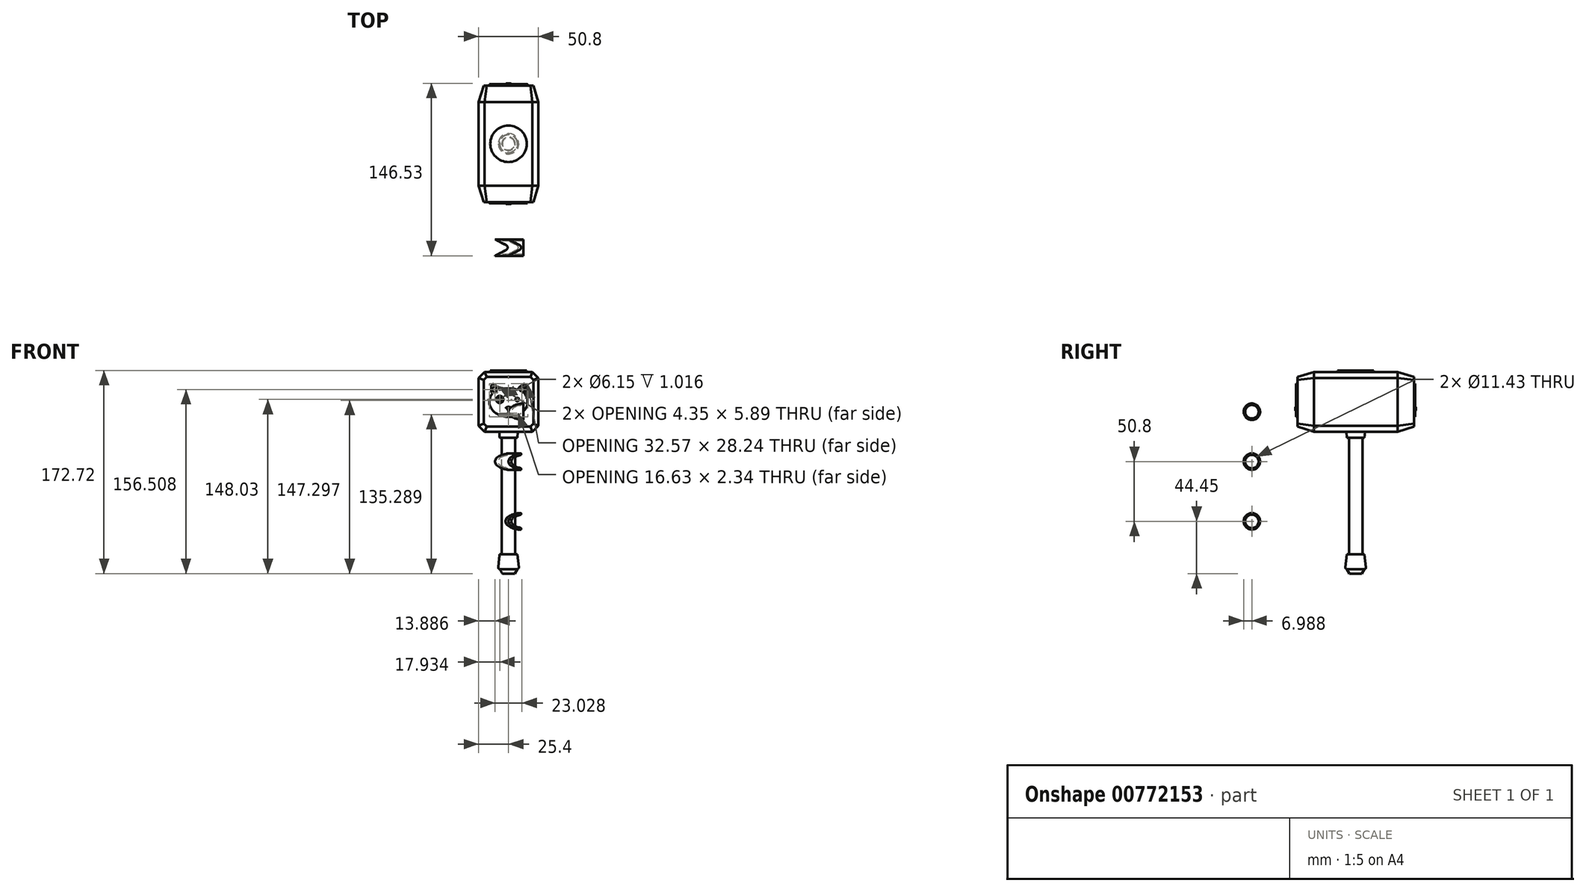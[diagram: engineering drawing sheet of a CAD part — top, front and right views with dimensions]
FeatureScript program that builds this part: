
annotation { "Feature Type Name" : "Feature", "Feature Type Description" : "" }
export const myFeature = defineFeature(function(context is Context, id is Id, definition is map)
    precondition{}
    {
        {
            var Q0;
            Q0=qCreatedBy(makeId("Front.planeOp"),FACE);
            var sketch = newSketch(context, id + "F0", { "sketchPlane" : qUnion([Q0])});
            skLineSegment(sketch, "E0.rect.bottom", {"start": v(25.4, 25.4) * mm, "end": v(-25.4, 25.4) * mm});
            skLineSegment(sketch, "E0.rect.top", {"start": v(25.4, -25.4) * mm, "end": v(-25.4, -25.4) * mm});
            skLineSegment(sketch, "E0.rect.left", {"start": v(25.4, 25.4) * mm, "end": v(25.4, -25.4) * mm});
            skLineSegment(sketch, "E0.rect.right", {"start": v(-25.4, 25.4) * mm, "end": v(-25.4, -25.4) * mm});
            skPoint(sketch, "E0.rect.middle", {"position": v(0, 0) * mm});
            skSolve(sketch);
        }
        {
            var Q0;
            Q0=makeQuery(id+"F0.imprint","IMPRINT",FACE,{"disambiguationData":[TD([[makeQuery(id+"F0.imprint","IMPRINT",EDGE,{"derivedFrom":sQuery(id+"F0.wireOp",EDGE,"E0.rect.bottom")}),1.0]])]});
            extrude(context, id + "F1", {"entities" : qUnion([Q0]), "endBound" : BoundingType.SYMMETRIC, "depth" : 71.12 * mm});
        }
        {
            var Q0;
            Q0=makeQuery(id+"F1.opExtrude","SWEPT_EDGE",EDGE,{"disambiguationData":[OSD([sQuery(id+"F0.wireOp",EDGE,"E0.rect.bottom"),sQuery(id+"F0.wireOp",EDGE,"E0.rect.left")])]});
            var Q1;
            Q1=makeQuery(id+"F1.opExtrude","SWEPT_EDGE",EDGE,{"disambiguationData":[OSD([sQuery(id+"F0.wireOp",EDGE,"E0.rect.top"),sQuery(id+"F0.wireOp",EDGE,"E0.rect.left")])]});
            var Q2;
            Q2=makeQuery(id+"F1.opExtrude","SWEPT_EDGE",EDGE,{"disambiguationData":[OSD([sQuery(id+"F0.wireOp",EDGE,"E0.rect.top"),sQuery(id+"F0.wireOp",EDGE,"E0.rect.right")])]});
            var Q3;
            Q3=makeQuery(id+"F1.opExtrude","SWEPT_EDGE",EDGE,{"disambiguationData":[OSD([sQuery(id+"F0.wireOp",EDGE,"E0.rect.bottom"),sQuery(id+"F0.wireOp",EDGE,"E0.rect.right")])]});
            chamfer(context, id + "F2", {"entities" : qUnion([Q0, Q1, Q2, Q3]), "width" : 5.08 * mm, "tangentPropagation" : true});
        }
        {
            var Q0;
            Q0=makeQuery(id+"F1.opExtrude","CAP_FACE",FACE,{"disambiguationData":[OSD([sQuery(id+"F0.wireOp",EDGE,"E0.rect.bottom"),sQuery(id+"F0.wireOp",EDGE,"E0.rect.top"),sQuery(id+"F0.wireOp",EDGE,"E0.rect.left"),sQuery(id+"F0.wireOp",EDGE,"E0.rect.right")])],"isStart":false});
            var sketch = newSketch(context, id + "F3", { "sketchPlane" : qUnion([Q0])});
            skLineSegment(sketch, "E1.0.0", {"start": v(20.32, 25.4) * mm, "end": v(-20.32, 25.4) * mm});
            skLineSegment(sketch, "E1.0.1", {"start": v(-20.32, 25.4) * mm, "end": v(-25.4, 20.32) * mm});
            skLineSegment(sketch, "E1.0.2", {"start": v(-25.4, 20.32) * mm, "end": v(-25.4, -20.32) * mm});
            skLineSegment(sketch, "E1.0.3", {"start": v(-25.4, -20.32) * mm, "end": v(-20.32, -25.4) * mm});
            skLineSegment(sketch, "E1.0.4", {"start": v(-20.32, -25.4) * mm, "end": v(20.32, -25.4) * mm});
            skLineSegment(sketch, "E1.0.5", {"start": v(20.32, -25.4) * mm, "end": v(25.4, -20.32) * mm});
            skLineSegment(sketch, "E1.0.6", {"start": v(25.4, -20.32) * mm, "end": v(25.4, 20.32) * mm});
            skLineSegment(sketch, "E1.0.7", {"start": v(25.4, 20.32) * mm, "end": v(20.32, 25.4) * mm});
            skSolve(sketch);
        }
        {
            var Q0;
            Q0=makeQuery(id+"F1.opExtrude","CAP_FACE",FACE,{"disambiguationData":[OSD([sQuery(id+"F0.wireOp",EDGE,"E0.rect.bottom"),sQuery(id+"F0.wireOp",EDGE,"E0.rect.top"),sQuery(id+"F0.wireOp",EDGE,"E0.rect.left"),sQuery(id+"F0.wireOp",EDGE,"E0.rect.right")])],"isStart":false});
            var Q1;
            Q1=makeQuery(id+"F3.imprint","IMPRINT",FACE,{"disambiguationData":[TD([[makeQuery(id+"F3.imprint","IMPRINT",EDGE,{"derivedFrom":sQuery(id+"F3.wireOp",EDGE,"E1.0.0")}),1.0]])]});
            extrude(context, id + "F4", {"entities" : qUnion([Q0, Q1]), "operationType" : NewBodyOperationType.ADD, "depth" : 13.97 * mm, "hasDraft" : true, "draftAngle" : 17 * degree, "draftPullDirection" : true});
        }
        {
            var Q0;
            Q0=makeQuery(id+"F1.opExtrude","CAP_FACE",FACE,{"disambiguationData":[OSD([sQuery(id+"F0.wireOp",EDGE,"E0.rect.bottom"),sQuery(id+"F0.wireOp",EDGE,"E0.rect.top"),sQuery(id+"F0.wireOp",EDGE,"E0.rect.left"),sQuery(id+"F0.wireOp",EDGE,"E0.rect.right")])],"isStart":true});
            var sketch = newSketch(context, id + "F5", { "sketchPlane" : qUnion([Q0])});
            skLineSegment(sketch, "E2.0.0", {"start": v(25.4, -20.32) * mm, "end": v(25.4, 20.32) * mm});
            skLineSegment(sketch, "E2.0.1", {"start": v(25.4, 20.32) * mm, "end": v(20.32, 25.4) * mm});
            skLineSegment(sketch, "E2.0.2", {"start": v(20.32, 25.4) * mm, "end": v(-20.32, 25.4) * mm});
            skLineSegment(sketch, "E2.0.3", {"start": v(-20.32, 25.4) * mm, "end": v(-25.4, 20.32) * mm});
            skLineSegment(sketch, "E2.0.4", {"start": v(-25.4, 20.32) * mm, "end": v(-25.4, -20.32) * mm});
            skLineSegment(sketch, "E2.0.5", {"start": v(-25.4, -20.32) * mm, "end": v(-20.32, -25.4) * mm});
            skLineSegment(sketch, "E2.0.6", {"start": v(-20.32, -25.4) * mm, "end": v(20.32, -25.4) * mm});
            skLineSegment(sketch, "E2.0.7", {"start": v(20.32, -25.4) * mm, "end": v(25.4, -20.32) * mm});
            skSolve(sketch);
        }
        {
            var Q0;
            Q0=makeQuery(id+"F5.imprint","IMPRINT",FACE,{"disambiguationData":[TD([[makeQuery(id+"F5.imprint","IMPRINT",EDGE,{"derivedFrom":sQuery(id+"F5.wireOp",EDGE,"E2.0.0")}),-1.0]])]});
            extrude(context, id + "F6", {"entities" : qUnion([Q0]), "operationType" : NewBodyOperationType.ADD, "depth" : 13.97 * mm, "hasDraft" : true, "draftAngle" : 17 * degree, "draftPullDirection" : true});
        }
        {
            var Q0;
            Q0=makeQuery(id+"F1.opExtrude","SWEPT_FACE",FACE,{"disambiguationData":[OSD([sQuery(id+"F0.wireOp",EDGE,"E0.rect.bottom")])]});
            var sketch = newSketch(context, id + "F7", { "sketchPlane" : qUnion([Q0])});
            skCircle(sketch, "E3", {"center": v(0, 0) * mm, "radius": 15.5 * mm});
            skSolve(sketch);
        }
        {
            var Q0;
            Q0=qSketchRegion(id+"F7",true);
            extrude(context, id + "F8", {"entities" : qUnion([Q0]), "operationType" : NewBodyOperationType.ADD, "depth" : 1.27 * mm});
        }
        {
            var Q0;
            Q0=makeQuery(id+"F1.opExtrude","SWEPT_FACE",FACE,{"disambiguationData":[OSD([sQuery(id+"F0.wireOp",EDGE,"E0.rect.top")])]});
            var sketch = newSketch(context, id + "F9", { "sketchPlane" : qUnion([Q0])});
            skCircle(sketch, "E4", {"center": v(0, 0) * mm, "radius": 7.93 * mm});
            skSolve(sketch);
        }
        {
            var Q0;
            Q0=qSketchRegion(id+"F9",true);
            extrude(context, id + "F10", {"entities" : qUnion([Q0]), "operationType" : NewBodyOperationType.ADD, "depth" : 5.08 * mm, "hasDraft" : true, "draftAngle" : 5 * degree, "draftPullDirection" : true});
        }
        {
            var Q0;
            Q0=makeQuery(id+"F10.opExtrude","CAP_FACE",FACE,{"disambiguationData":[OSD([sQuery(id+"F9.wireOp",EDGE,"E4")])],"isStart":false});
            var sketch = newSketch(context, id + "F11", { "sketchPlane" : qUnion([Q0])});
            skCircle(sketch, "E5", {"center": v(0, 0) * mm, "radius": 6.99 * mm});
            skCircle(sketch, "E6", {"center": v(0, 0) * mm, "radius": 5.72 * mm});
            skSolve(sketch);
        }
        {
            var Q0;
            Q0=makeQuery(id+"F11.imprint","IMPRINT",FACE,{"disambiguationData":[TD([[makeQuery(id+"F11.imprint","IMPRINT",EDGE,{"derivedFrom":sQuery(id+"F11.wireOp",EDGE,"E6")}),1.0]])]});
            extrude(context, id + "F12", {"entities" : qUnion([Q0]), "operationType" : NewBodyOperationType.ADD, "depth" : 99.06 * mm});
        }
        {
            var Q0;
            Q0=makeQuery(id+"F12.opExtrude","CAP_FACE",FACE,{"disambiguationData":[OSD([sQuery(id+"F11.wireOp",EDGE,"E6")])],"isStart":false});
            var sketch = newSketch(context, id + "F13", { "sketchPlane" : qUnion([Q0])});
            skCircle(sketch, "E7", {"center": v(0, 0) * mm, "radius": 7.55 * mm});
            skSolve(sketch);
        }
        {
            var Q0;
            Q0=qSketchRegion(id+"F13",true);
            extrude(context, id + "F14", {"entities" : qUnion([Q0]), "depth" : 12.7 * mm, "hasDraft" : true, "draftAngle" : 6 * degree});
        }
        {
            var Q0;
            Q0=makeQuery(id+"F14.opExtrude","CAP_EDGE",EDGE,{"disambiguationData":[OSD([sQuery(id+"F13.wireOp",EDGE,"E7")])],"isStart":false});
            fillet(context, id + "F15", {"entities" : qUnion([Q0]), "radius" : 1.27 * mm, "tangentPropagation" : true, "allowEdgeOverflow" : false});
        }
        {
            var Q0;
            Q0=makeQuery(id+"F14.opExtrude","CAP_FACE",FACE,{"disambiguationData":[OSD([sQuery(id+"F13.wireOp",EDGE,"E7")])],"isStart":false});
            var sketch = newSketch(context, id + "F16", { "sketchPlane" : qUnion([Q0])});
            skCircle(sketch, "E8.0", {"center": v(0, 0) * mm, "radius": 7.47 * mm});
            skSolve(sketch);
        }
        {
            var Q0;
            Q0=qSketchRegion(id+"F16",true);
            extrude(context, id + "F17", {"entities" : qUnion([Q0]), "operationType" : NewBodyOperationType.ADD, "depth" : 3.8 * mm, "hasDraft" : true, "draftAngle" : 30 * degree, "draftPullDirection" : true});
        }
        {
            var Q0;
            Q0=qCreatedBy(makeId("Right.planeOp"),FACE);
            var sketch = newSketch(context, id + "F18", { "sketchPlane" : qUnion([Q0])});
            skCircle(sketch, "E9", {"center": v(-88.23, -8.44) * mm, "radius": 6.99 * mm});
            skCircle(sketch, "E10", {"center": v(-88.23, -8.44) * mm, "radius": 5.72 * mm});
            skSolve(sketch);
        }
        {
            var Q0;
            Q0=qSketchRegion(id+"F18",true);
            extrude(context, id + "F19", {"entities" : qUnion([Q0]), "depth" : 12.7 * mm});
        }
        {
            var Q0;
            Q0=qCreatedBy(makeId("Top.planeOp"),FACE);
            var sketch = newSketch(context, id + "F20", { "sketchPlane" : qUnion([Q0])});
            skLineSegment(sketch, "E11.0", {"start": v(12.7, -81.25) * mm, "end": v(12.7, -95.22) * mm});
            skLineSegment(sketch, "E12.0", {"start": v(0, -81.25) * mm, "end": v(0, -88.23) * mm});
            skLineSegment(sketch, "E13", {"start": v(0, -81.25) * mm, "end": v(9.4, -86.15) * mm});
            skLineSegment(sketch, "E14.MirrorCS", {"start": v(0, -95.22) * mm, "end": v(9.4, -90.31) * mm});
            skArc(sketch, "E15", {"start": v(9.4, -90.31) * mm, "mid": v(10.65, -88.23) * mm, "end": v(9.4, -86.15) * mm});
            skPoint(sketch, "E16.orphan", {"position": v(0, -95.22) * mm});
            skLineSegment(sketch, "E17", {"start": v(0, -88.23) * mm, "end": v(0, -95.22) * mm});
            skLineSegment(sketch, "E18", {"start": v(0, -95.22) * mm, "end": v(-11.43, -95.22) * mm});
            skLineSegment(sketch, "E19", {"start": v(0, -81.25) * mm, "end": v(-11.43, -81.25) * mm});
            skLineSegment(sketch, "E20", {"start": v(-11.43, -95.22) * mm, "end": v(-2.04, -90.31) * mm});
            skLineSegment(sketch, "E21", {"start": v(0, -88.23) * mm, "end": v(8.3, -88.23) * mm});
            skLineSegment(sketch, "E22.MirrorCS", {"start": v(-11.43, -81.25) * mm, "end": v(-2.04, -86.15) * mm});
            skArc(sketch, "E23", {"start": v(-2.04, -90.31) * mm, "mid": v(-0.78, -88.23) * mm, "end": v(-2.04, -86.15) * mm});
            skSolve(sketch);
        }
        {
            var Q0;
            Q0=qSketchRegion(id+"F20",true);
            extrude(context, id + "F21", {"entities" : qUnion([Q0]), "operationType" : NewBodyOperationType.REMOVE, "oppositeDirection" : true, "depth" : 25.4 * mm});
        }
        {
            var Q0;
            Q0=qCreatedBy(makeId("Right.planeOp"),FACE);
            var sketch = newSketch(context, id + "F22", { "sketchPlane" : qUnion([Q0])});
            skCircle(sketch, "E24.0", {"center": v(-88.23, -8.44) * mm, "radius": 5.72 * mm});
            skLineSegment(sketch, "E25", {"start": v(-88.23, -8.44) * mm, "end": v(-88.23, 15.5) * mm});
            skCircle(sketch, "E26", {"center": v(-88.23, 15.5) * mm, "radius": 6.99 * mm});
            skCircle(sketch, "E27", {"center": v(-88.23, 15.5) * mm, "radius": 5.72 * mm});
            skSolve(sketch);
        }
        {
            var Q0;
            Q0=makeQuery(id+"F22.imprint","IMPRINT",FACE,{"disambiguationData":[TD([[makeQuery(id+"F22.imprint","IMPRINT",EDGE,{"derivedFrom":sQuery(id+"F22.wireOp",EDGE,"E26")}),1.0]])]});
            extrude(context, id + "F23", {"entities" : qUnion([Q0]), "endBound" : BoundingType.SYMMETRIC, "depth" : 22.86 * mm});
        }
        {
            var Q0;
            Q0=qSketchRegion(id+"F20",true);
            extrude(context, id + "F24", {"entities" : qUnion([Q0]), "operationType" : NewBodyOperationType.REMOVE, "endBound" : BoundingType.SYMMETRIC, "oppositeDirection" : true, "depth" : 508 * mm});
        }
        {
            var Q0;
            Q0=makeQuery(id+"F24.boolean.opBoolean","SPLIT",BODY,{"disambiguationData":[OD(0.0)],"derivedFrom":makeQuery(id+"F23.opExtrude","SWEPT_BODY",BODY,{"disambiguationData":[OSD([sQuery(id+"F22.wireOp",EDGE,"E26"),sQuery(id+"F22.wireOp",EDGE,"E27")])]})});
            deleteBodies(context, id + "F25", {"entities" : qUnion([Q0])});
        }
        {
            var Q0;
            Q0=qCreatedBy(makeId("Right.planeOp"),FACE);
            var sketch = newSketch(context, id + "F26", { "sketchPlane" : qUnion([Q0])});
            skCircle(sketch, "E28.0", {"center": v(-88.23, -8.44) * mm, "radius": 5.72 * mm});
            skLineSegment(sketch, "E29", {"start": v(-88.23, -8.44) * mm, "end": v(-88.23, -50.8) * mm});
            skLineSegment(sketch, "E30", {"start": v(0, 0) * mm, "end": v(-109.96, 0) * mm});
            skCircle(sketch, "E31", {"center": v(-88.23, -50.8) * mm, "radius": 6.99 * mm});
            skCircle(sketch, "E32", {"center": v(-88.23, -50.8) * mm, "radius": 5.72 * mm});
            skSolve(sketch);
        }
        {
            var Q0;
            Q0=makeQuery(id+"F26.imprint","IMPRINT",FACE,{"disambiguationData":[TD([[makeQuery(id+"F26.imprint","IMPRINT",EDGE,{"derivedFrom":sQuery(id+"F26.wireOp",EDGE,"E31")}),1.0]])]});
            extrude(context, id + "F27", {"entities" : qUnion([Q0]), "endBound" : BoundingType.SYMMETRIC, "depth" : 25.4 * mm});
        }
        {
            var Q0;
            Q0=qCreatedBy(makeId("Top.planeOp"),FACE);
            cPlane(context, id + "F28", {"entities" : qUnion([Q0]), "cplaneType" : CPlaneType.OFFSET, "offset" : 50.8 * mm, "oppositeDirection" : true, "width" : 152.4 * mm, "height" : 152.4 * mm});
        }
        {
            var Q0;
            Q0=qCreatedBy(id+"F28.planeOp",FACE);
            var sketch = newSketch(context, id + "F29", { "sketchPlane" : qUnion([Q0])});
            skLineSegment(sketch, "E33.0", {"start": v(9.4, -86.15) * mm, "end": v(0, -81.25) * mm});
            skArc(sketch, "E34.0", {"start": v(9.4, -86.15) * mm, "mid": v(10.65, -88.23) * mm, "end": v(9.4, -90.31) * mm});
            skLineSegment(sketch, "E35.0", {"start": v(9.4, -90.31) * mm, "end": v(0, -95.22) * mm});
            skLineSegment(sketch, "E36", {"start": v(12.7, -95.22) * mm, "end": v(0, -95.22) * mm});
            skLineSegment(sketch, "E37.0", {"start": v(12.7, -81.25) * mm, "end": v(12.7, -95.22) * mm});
            skLineSegment(sketch, "E38", {"start": v(0, -81.25) * mm, "end": v(12.7, -81.25) * mm});
            skLineSegment(sketch, "E39.0", {"start": v(-12.7, -81.25) * mm, "end": v(-12.7, -95.22) * mm});
            skArc(sketch, "E40.0", {"start": v(-2.04, -86.15) * mm, "mid": v(-0.78, -88.23) * mm, "end": v(-2.04, -90.31) * mm});
            skLineSegment(sketch, "E41.0", {"start": v(-2.04, -86.15) * mm, "end": v(-11.43, -81.25) * mm});
            skLineSegment(sketch, "E42.0", {"start": v(-2.04, -90.31) * mm, "end": v(-11.43, -95.22) * mm});
            skLineSegment(sketch, "E43", {"start": v(-11.43, -81.25) * mm, "end": v(-12.7, -81.25) * mm});
            skLineSegment(sketch, "E44", {"start": v(-11.43, -95.22) * mm, "end": v(-12.7, -95.22) * mm});
            skSolve(sketch);
        }
        {
            var Q0;
            Q0=qSketchRegion(id+"F29",true);
            extrude(context, id + "F30", {"entities" : qUnion([Q0]), "operationType" : NewBodyOperationType.REMOVE, "endBound" : BoundingType.SYMMETRIC, "oppositeDirection" : true, "depth" : 25.4 * mm});
        }
        {
            var Q0;
            Q0=qCreatedBy(makeId("Right.planeOp"),FACE);
            var sketch = newSketch(context, id + "F31", { "sketchPlane" : qUnion([Q0])});
            skArc(sketch, "E45.0", {"start": v(-86.15, -56.12) * mm, "mid": v(-82.52, -50.8) * mm, "end": v(-86.15, -45.48) * mm});
            skLineSegment(sketch, "E46", {"start": v(-88.23, -50.8) * mm, "end": v(-88.23, -101.6) * mm});
            skCircle(sketch, "E47", {"center": v(-88.23, -101.6) * mm, "radius": 6.99 * mm});
            skCircle(sketch, "E48", {"center": v(-88.23, -101.6) * mm, "radius": 5.72 * mm});
            skSolve(sketch);
        }
        {
            var Q0;
            Q0=makeQuery(id+"F31.imprint","IMPRINT",FACE,{"disambiguationData":[TD([[makeQuery(id+"F31.imprint","IMPRINT",EDGE,{"derivedFrom":sQuery(id+"F31.wireOp",EDGE,"E47")}),1.0]])]});
            extrude(context, id + "F32", {"entities" : qUnion([Q0]), "endBound" : BoundingType.SYMMETRIC, "depth" : 25.4 * mm});
        }
        {
            var Q0;
            Q0=qCreatedBy(id+"F28.planeOp",FACE);
            cPlane(context, id + "F33", {"entities" : qUnion([Q0]), "cplaneType" : CPlaneType.OFFSET, "offset" : 50.8 * mm, "oppositeDirection" : true, "width" : 152.4 * mm, "height" : 152.4 * mm});
        }
        {
            var Q0;
            Q0=qCreatedBy(id+"F33.planeOp",FACE);
            var sketch = newSketch(context, id + "F34", { "sketchPlane" : qUnion([Q0])});
            skLineSegment(sketch, "E49.0", {"start": v(9.4, -86.15) * mm, "end": v(0, -81.25) * mm});
            skArc(sketch, "E50.0", {"start": v(9.4, -86.15) * mm, "mid": v(10.65, -88.23) * mm, "end": v(9.4, -90.31) * mm});
            skLineSegment(sketch, "E51.0", {"start": v(9.4, -90.31) * mm, "end": v(0, -95.22) * mm});
            skLineSegment(sketch, "E52", {"start": v(-2.54, -95.22) * mm, "end": v(-2.54, -81.25) * mm});
            skLineSegment(sketch, "E53", {"start": v(-2.54, -95.22) * mm, "end": v(6.85, -90.31) * mm});
            skLineSegment(sketch, "E54.MirrorCS", {"start": v(-2.54, -81.25) * mm, "end": v(6.85, -86.15) * mm});
            skPoint(sketch, "E55.end.orphan", {"position": v(-2.54, -88.23) * mm});
            skArc(sketch, "E56", {"start": v(6.85, -90.31) * mm, "mid": v(8.11, -88.23) * mm, "end": v(6.85, -86.15) * mm});
            skLineSegment(sketch, "E57", {"start": v(-2.54, -95.22) * mm, "end": v(-16.11, -102.03) * mm});
            skLineSegment(sketch, "E58", {"start": v(-16.11, -102.03) * mm, "end": v(-15.24, -76.78) * mm});
            skLineSegment(sketch, "E59", {"start": v(-15.24, -76.78) * mm, "end": v(-2.54, -81.25) * mm});
            skLineSegment(sketch, "E60", {"start": v(0, -95.22) * mm, "end": v(15.67, -96.34) * mm});
            skLineSegment(sketch, "E61", {"start": v(15.67, -96.34) * mm, "end": v(14.05, -78.86) * mm});
            skLineSegment(sketch, "E62", {"start": v(14.05, -78.86) * mm, "end": v(0, -81.25) * mm});
            skSolve(sketch);
        }
        {
            var Q0;
            Q0=qSketchRegion(id+"F34",true);
            extrude(context, id + "F35", {"entities" : qUnion([Q0]), "operationType" : NewBodyOperationType.REMOVE, "endBound" : BoundingType.SYMMETRIC, "oppositeDirection" : true, "depth" : 25.4 * mm});
        }
        {
            var Q0;
            Q0=makeQuery(id+"F4.opExtrude","CAP_FACE",FACE,{"disambiguationData":[OSD([sQuery(id+"F0.wireOp",EDGE,"E0.rect.bottom"),sQuery(id+"F0.wireOp",EDGE,"E0.rect.top"),sQuery(id+"F0.wireOp",EDGE,"E0.rect.left"),sQuery(id+"F0.wireOp",EDGE,"E0.rect.right")])],"isStart":false});
            var sketch = newSketch(context, id + "F36", { "sketchPlane" : qUnion([Q0])});
            skEllipticalArc(sketch, "E63", {});
            skPoint(sketch, "E64", {"position": v(-13.78, 6.87) * mm});
            skLineSegment(sketch, "E65", {"start": v(0, 0) * mm, "end": v(0, 5.05) * mm});
            skPoint(sketch, "E66", {"position": v(0, -12.87) * mm});
            skPoint(sketch, "E67.MirrorP", {"position": v(13.78, 6.87) * mm});
            skLineSegment(sketch, "E68", {"start": v(0, -12.87) * mm, "end": v(0, -12.87) * mm});
            skEllipticalArc(sketch, "E69.trimOffspring", {});
            skPoint(sketch, "E70", {"position": v(-7.9, 10.08) * mm});
            skPoint(sketch, "E71.MirrorP", {"position": v(7.9, 10.08) * mm});
            skArc(sketch, "E72", {"start": v(-13.78, 15.37) * mm, "mid": v(-14.79, 11.12) * mm, "end": v(-13.78, 6.87) * mm});
            skArc(sketch, "E73", {"start": v(-7.9, 10.08) * mm, "mid": v(-10.29, 13.34) * mm, "end": v(-13.78, 15.37) * mm});
            skArc(sketch, "E74.MirrorCS", {"start": v(7.9, 10.08) * mm, "mid": v(10.29, 13.34) * mm, "end": v(13.78, 15.37) * mm});
            skArc(sketch, "E75.MirrorCS", {"start": v(13.78, 15.37) * mm, "mid": v(14.79, 11.12) * mm, "end": v(13.78, 6.87) * mm});
            skArc(sketch, "E76", {"start": v(-13.25, 13.4) * mm, "mid": v(-13.68, 10.42) * mm, "end": v(-12.89, 7.51) * mm});
            skArc(sketch, "E77", {"start": v(-9.34, 9.5) * mm, "mid": v(-11.04, 11.7) * mm, "end": v(-13.25, 13.4) * mm});
            skArc(sketch, "E78.MirrorCS", {"start": v(9.34, 9.5) * mm, "mid": v(11.04, 11.7) * mm, "end": v(13.25, 13.4) * mm});
            skArc(sketch, "E79.MirrorCS", {"start": v(13.25, 13.4) * mm, "mid": v(13.68, 10.42) * mm, "end": v(12.89, 7.51) * mm});
            skArc(sketch, "E80.trimOffspring", {"start": v(7.9, 10.08) * mm, "mid": v(0, 11.5) * mm, "end": v(-7.9, 10.08) * mm});
            skLineSegment(sketch, "E81", {"start": v(0, 2.53) * mm, "end": v(-7.47, 1.98) * mm});
            skCircle(sketch, "E82", {"center": v(-7.47, 1.98) * mm, "radius": 3.07 * mm});
            skCircle(sketch, "E83", {"center": v(-7.47, 1.98) * mm, "radius": 1.55 * mm});
            skCircle(sketch, "E84.MirrorC", {"center": v(7.47, 1.98) * mm, "radius": 1.55 * mm});
            skCircle(sketch, "E85.MirrorC", {"center": v(7.47, 1.98) * mm, "radius": 3.07 * mm});
            skArc(sketch, "E86", {"start": v(-8.55, -10.96) * mm, "mid": v(-4.2, -10.8) * mm, "end": v(0, -9.6) * mm});
            skArc(sketch, "E87", {"start": v(-8.55, -10.96) * mm, "mid": v(-4.31, -11.98) * mm, "end": v(0, -11.35) * mm});
            skArc(sketch, "E88.MirrorCS", {"start": v(8.55, -10.96) * mm, "mid": v(4.2, -10.8) * mm, "end": v(0, -9.6) * mm});
            skArc(sketch, "E89.MirrorCS", {"start": v(8.55, -10.96) * mm, "mid": v(4.31, -11.98) * mm, "end": v(0, -11.35) * mm});
            skArc(sketch, "E90", {"start": v(-9.34, 9.5) * mm, "mid": v(-11.24, 8.73) * mm, "end": v(-12.89, 7.51) * mm});
            skArc(sketch, "E91.MirrorCS", {"start": v(9.34, 9.5) * mm, "mid": v(11.24, 8.73) * mm, "end": v(12.89, 7.51) * mm});
            skArc(sketch, "E92", {"start": v(-0.22, -7.54) * mm, "mid": v(-0.39, -7.2) * mm, "end": v(-0.58, -6.89) * mm});
            skArc(sketch, "E93.MirrorCS", {"start": v(0.22, -7.54) * mm, "mid": v(0.39, -7.2) * mm, "end": v(0.58, -6.89) * mm});
            skArc(sketch, "E94", {"start": v(-0.6, -6.68) * mm, "mid": v(-0.73, -6.02) * mm, "end": v(-1.36, -5.8) * mm});
            skArc(sketch, "E95.trimOffspring", {"start": v(-1.56, -5.74) * mm, "mid": v(-1.84, -5.52) * mm, "end": v(-2.13, -5.31) * mm});
            skArc(sketch, "E96", {"start": v(2.1, -4.89) * mm, "mid": v(0, -4.32) * mm, "end": v(-2.12, -4.9) * mm});
            skArc(sketch, "E97.MirrorCS", {"start": v(0.6, -6.68) * mm, "mid": v(0.73, -6.02) * mm, "end": v(1.36, -5.8) * mm});
            skArc(sketch, "E98.trimOffspring", {"start": v(1.56, -5.74) * mm, "mid": v(1.83, -5.52) * mm, "end": v(2.12, -5.32) * mm});
            skPoint(sketch, "E99.visualSharp", {"position": v(-2.45, -5.12) * mm});
            skArc(sketch, "E99.filletArc", {"start": v(-2.12, -4.9) * mm, "mid": v(-2.24, -5.1) * mm, "end": v(-2.13, -5.31) * mm});
            skPoint(sketch, "E100.visualSharp", {"position": v(-1.47, -5.82) * mm});
            skArc(sketch, "E100.filletArc", {"start": v(-1.56, -5.74) * mm, "mid": v(-1.47, -5.8) * mm, "end": v(-1.36, -5.8) * mm});
            skPoint(sketch, "E101.visualSharp", {"position": v(-0.64, -6.78) * mm});
            skArc(sketch, "E101.filletArc", {"start": v(-0.6, -6.68) * mm, "mid": v(-0.61, -6.78) * mm, "end": v(-0.58, -6.89) * mm});
            skPoint(sketch, "E102.visualSharp", {"position": v(0, -8.1) * mm});
            skArc(sketch, "E102.filletArc", {"start": v(-0.22, -7.54) * mm, "mid": v(0, -7.68) * mm, "end": v(0.22, -7.54) * mm});
            skPoint(sketch, "E103.visualSharp", {"position": v(0.64, -6.78) * mm});
            skArc(sketch, "E103.filletArc", {"start": v(0.58, -6.89) * mm, "mid": v(0.61, -6.78) * mm, "end": v(0.6, -6.68) * mm});
            skPoint(sketch, "E104.visualSharp", {"position": v(1.47, -5.82) * mm});
            skArc(sketch, "E104.filletArc", {"start": v(1.36, -5.8) * mm, "mid": v(1.47, -5.8) * mm, "end": v(1.56, -5.74) * mm});
            skPoint(sketch, "E105.visualSharp", {"position": v(2.45, -5.12) * mm});
            skArc(sketch, "E105.filletArc", {"start": v(2.12, -5.32) * mm, "mid": v(2.23, -5.1) * mm, "end": v(2.1, -4.89) * mm});
            const initialGuessF36  = {"E63": [0, 0, -1, 0, 0.016292555257678032, 0.012874885158971939, 1.5707963267948966, 3.7046613959133827], "E69.trimOffspring": [0, 0, -1, 0, 0.016292555257678032, 0.012874885158971939, 5.720116564855996, 1.5707963267948966]};
            skSetInitialGuess(sketch, initialGuessF36);
            skSolve(sketch);
        }
        {
            var Q0;
            {var subQ4=sQuery(id+"F36.wireOp",EDGE,"E72");Q0=makeQuery(id+"F36.imprint","IMPRINT",FACE,{"disambiguationData":[TD([[makeQuery(id+"F36.imprint","IMPRINT",EDGE,{"derivedFrom":subQ4}),1.0]])]});}
            var Q1;
            Q1=makeQuery(id+"F36.imprint","IMPRINT",FACE,{"disambiguationData":[TD([[makeQuery(id+"F36.imprint","IMPRINT",EDGE,{"derivedFrom":sQuery(id+"F36.wireOp",EDGE,"E83")}),1.0]])]});
            var Q2;
            Q2=makeQuery(id+"F36.imprint","IMPRINT",FACE,{"disambiguationData":[TD([[makeQuery(id+"F36.imprint","IMPRINT",EDGE,{"derivedFrom":sQuery(id+"F36.wireOp",EDGE,"E84.MirrorC")}),-1.0]])]});
            extrude(context, id + "F37", {"entities" : qUnion([Q0, Q1, Q2]), "operationType" : NewBodyOperationType.ADD, "depth" : 1.02 * mm});
        }
        {
            var Q0;
            Q0=makeQuery(id+"F36.imprint","IMPRINT",FACE,{"disambiguationData":[TD([[makeQuery(id+"F36.imprint","IMPRINT",EDGE,{"derivedFrom":sQuery(id+"F36.wireOp",EDGE,"E92")}),-1.0]])]});
            extrude(context, id + "F38", {"entities" : qUnion([Q0]), "operationType" : NewBodyOperationType.ADD, "depth" : 1.78 * mm});
        }
        {
            var Q0;
            Q0=makeQuery(id+"F38.opExtrude","CAP_EDGE",EDGE,{"disambiguationData":[OSD([sQuery(id+"F36.wireOp",EDGE,"E105.filletArc")])],"isStart":false});
            var Q1;
            Q1=makeQuery(id+"F38.opExtrude","CAP_EDGE",EDGE,{"disambiguationData":[OSD([sQuery(id+"F36.wireOp",EDGE,"E96")])],"isStart":false});
            var Q2;
            Q2=makeQuery(id+"F38.opExtrude","CAP_EDGE",EDGE,{"disambiguationData":[OSD([sQuery(id+"F36.wireOp",EDGE,"E99.filletArc")])],"isStart":false});
            var Q3;
            Q3=makeQuery(id+"F38.opExtrude","CAP_EDGE",EDGE,{"disambiguationData":[OSD([sQuery(id+"F36.wireOp",EDGE,"E95.trimOffspring")])],"isStart":false});
            var Q4;
            Q4=makeQuery(id+"F38.opExtrude","CAP_EDGE",EDGE,{"disambiguationData":[OSD([sQuery(id+"F36.wireOp",EDGE,"E97.MirrorCS")])],"isStart":false});
            var Q5;
            Q5=makeQuery(id+"F38.opExtrude","CAP_EDGE",EDGE,{"disambiguationData":[OSD([sQuery(id+"F36.wireOp",EDGE,"E98.trimOffspring")])],"isStart":false});
            var Q6;
            Q6=makeQuery(id+"F38.opExtrude","CAP_EDGE",EDGE,{"disambiguationData":[OSD([sQuery(id+"F36.wireOp",EDGE,"E104.filletArc")])],"isStart":false});
            var Q7;
            Q7=makeQuery(id+"F38.opExtrude","CAP_FACE",FACE,{"disambiguationData":[OSD([sQuery(id+"F36.wireOp",EDGE,"E92"),sQuery(id+"F36.wireOp",EDGE,"E93.MirrorCS"),sQuery(id+"F36.wireOp",EDGE,"E94"),sQuery(id+"F36.wireOp",EDGE,"E95.trimOffspring"),sQuery(id+"F36.wireOp",EDGE,"E96"),sQuery(id+"F36.wireOp",EDGE,"E97.MirrorCS"),sQuery(id+"F36.wireOp",EDGE,"E98.trimOffspring"),sQuery(id+"F36.wireOp",EDGE,"E99.filletArc"),sQuery(id+"F36.wireOp",EDGE,"E100.filletArc"),sQuery(id+"F36.wireOp",EDGE,"E101.filletArc"),sQuery(id+"F36.wireOp",EDGE,"E102.filletArc"),sQuery(id+"F36.wireOp",EDGE,"E103.filletArc"),sQuery(id+"F36.wireOp",EDGE,"E104.filletArc"),sQuery(id+"F36.wireOp",EDGE,"E105.filletArc")])],"isStart":false});
            fillet(context, id + "F39", {"entities" : qUnion([Q0, Q1, Q2, Q3, Q4, Q5, Q6, Q7]), "radius" : 0.5 * mm, "tangentPropagation" : true, "allowEdgeOverflow" : false});
        }
        {
            var Q0;
            {var subQ0=sQuery(id+"F0.wireOp",EDGE,"E0.rect.bottom");var subQ1=sQuery(id+"F0.wireOp",EDGE,"E0.rect.top");var subQ2=sQuery(id+"F0.wireOp",EDGE,"E0.rect.left");var subQ3=sQuery(id+"F0.wireOp",EDGE,"E0.rect.right");Q0=makeQuery(id+"F37.boolean.opBoolean","SPLIT",FACE,{"disambiguationData":[TD([makeQuery(id+"F4.opExtrude","SWEPT_FACE",FACE,{"disambiguationData":[OSD([subQ0])]})])],"derivedFrom":makeQuery(id+"F4.opExtrude","CAP_FACE",FACE,{"disambiguationData":[OSD([subQ0,subQ1,subQ2,subQ3])],"isStart":false})});}
            var sketch = newSketch(context, id + "F40", { "sketchPlane" : qUnion([Q0])});
            skEllipticalArc(sketch, "E106.0", {});
            skEllipticalArc(sketch, "E107.0", {});
            skArc(sketch, "E108", {"start": v(-8.31, -10.98) * mm, "mid": v(-4.2, -11.93) * mm, "end": v(0, -11.35) * mm});
            skLineSegment(sketch, "E109", {"start": v(0, -11.35) * mm, "end": v(0, -12.87) * mm});
            skPoint(sketch, "E110.0.start.orphan", {"position": v(-8.55, -10.96) * mm});
            skPoint(sketch, "E111.0.end.orphan", {"position": v(0, -11.35) * mm});
            skPoint(sketch, "E111.0.start.orphan", {"position": v(8.55, -10.96) * mm});
            skArc(sketch, "E112.MirrorCS", {"start": v(8.31, -10.98) * mm, "mid": v(4.2, -11.93) * mm, "end": v(0, -11.35) * mm});
            skLineSegment(sketch, "E113", {"start": v(-8.31, -10.98) * mm, "end": v(-8.55, -10.96) * mm});
            skLineSegment(sketch, "E114", {"start": v(8.31, -10.98) * mm, "end": v(8.55, -10.96) * mm});
            const initialGuessF40  = {"E106.0": [0, 0, -1, 0, 0.016292555257678032, 0.012874885158971939, 5.720116564855996, 1.5707963267948966], "E107.0": [0, 0, -1, 0, 0.016292555257678032, 0.012874885158971939, 1.5707963267948966, 3.7046613959133823]};
            skSetInitialGuess(sketch, initialGuessF40);
            skSolve(sketch);
        }
        {
            var Q0;
            Q0=qSketchRegion(id+"F40",true);
            extrude(context, id + "F41", {"entities" : qUnion([Q0]), "operationType" : NewBodyOperationType.ADD, "depth" : 1.02 * mm});
        }
        {
            var Q0;
            Q0=qCreatedBy(makeId("Right.planeOp"),FACE);
            var sketch = newSketch(context, id + "F42", { "sketchPlane" : qUnion([Q0])});
            skLineSegment(sketch, "E115", {"start": v(0, 0) * mm, "end": v(0, -126) * mm});
            skLineSegment(sketch, "E116.0", {"start": v(7.55, -129.54) * mm, "end": v(-7.55, -129.54) * mm});
            skLineSegment(sketch, "E117", {"start": v(0, -126) * mm, "end": v(0, -129.54) * mm});
            skLineSegment(sketch, "E118", {"start": v(0, -129.54) * mm, "end": v(78.8, -129.54) * mm});
            skLineSegment(sketch, "E119", {"start": v(78.8, -129.54) * mm, "end": v(78.8, 49.1) * mm});
            skLineSegment(sketch, "E120", {"start": v(78.8, 49.1) * mm, "end": v(0, 49.1) * mm});
            skLineSegment(sketch, "E121", {"start": v(0, 49.1) * mm, "end": v(0, 0) * mm});
            skSolve(sketch);
        }
        {
            var Q0;
            Q0=qSketchRegion(id+"F42",true);
            extrude(context, id + "F43", {"entities" : qUnion([Q0]), "operationType" : NewBodyOperationType.REMOVE, "endBound" : BoundingType.SYMMETRIC, "oppositeDirection" : true, "depth" : 101.6 * mm});
        }
        {
            var Q0;
            Q0=makeQuery(id+"F1.opExtrude","SWEPT_BODY",BODY,{"disambiguationData":[OSD([sQuery(id+"F0.wireOp",EDGE,"E0.rect.bottom"),sQuery(id+"F0.wireOp",EDGE,"E0.rect.top"),sQuery(id+"F0.wireOp",EDGE,"E0.rect.left"),sQuery(id+"F0.wireOp",EDGE,"E0.rect.right")])]});
            var Q1;
            Q1=makeQuery(id+"F43.boolean.opBoolean","COPY",FACE,{"derivedFrom":makeQuery(id+"F43.opExtrude","SWEPT_FACE",FACE,{"disambiguationData":[OSD([sQuery(id+"F42.wireOp",EDGE,"E115"),sQuery(id+"F42.wireOp",EDGE,"E117"),sQuery(id+"F42.wireOp",EDGE,"E121")])]})});
            mirror(context, id + "F44", {"operationType" : NewBodyOperationType.ADD, "entities" : qUnion([Q0]), "mirrorPlane" : qUnion([Q1])});
        }
    });
